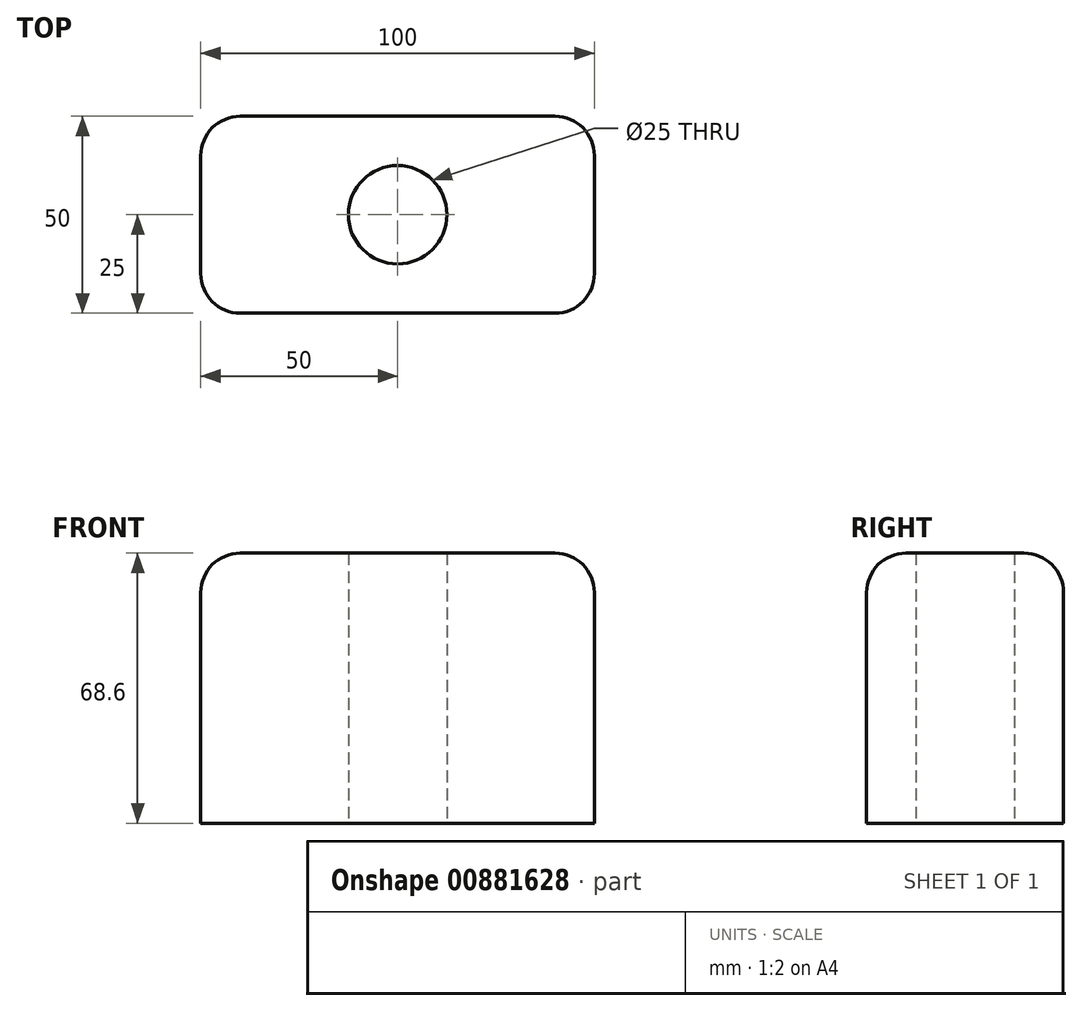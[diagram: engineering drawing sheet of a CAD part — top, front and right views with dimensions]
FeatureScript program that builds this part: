
annotation { "Feature Type Name" : "Feature", "Feature Type Description" : "" }
export const myFeature = defineFeature(function(context is Context, id is Id, definition is map)
    precondition{}
    {
        {
            var Q0;
            Q0=qCreatedBy(makeId("Top.planeOp"),FACE);
            var sketch = newSketch(context, id + "F0", { "sketchPlane" : qUnion([Q0])});
            skLineSegment(sketch, "E0.bottom", {"start": v(-50, 25) * mm, "end": v(50, 25) * mm});
            skLineSegment(sketch, "E0.top", {"start": v(-50, -25) * mm, "end": v(50, -25) * mm});
            skLineSegment(sketch, "E0.left", {"start": v(-50, 25) * mm, "end": v(-50, -25) * mm});
            skLineSegment(sketch, "E0.right", {"start": v(50, 25) * mm, "end": v(50, -25) * mm});
            skPoint(sketch, "E1", {"position": v(-50, 0) * mm});
            skPoint(sketch, "E2", {"position": v(0, 25) * mm});
            skCircle(sketch, "E3", {"center": v(0, 0) * mm, "radius": 12.5 * mm});
            skSolve(sketch);
        }
        {
            var Q0;
            Q0=makeQuery(id+"F0.imprint","IMPRINT",FACE,{"disambiguationData":[TD([[makeQuery(id+"F0.imprint","IMPRINT",EDGE,{"derivedFrom":sQuery(id+"F0.wireOp",EDGE,"E0.bottom")}),-1.0]])]});
            extrude(context, id + "F1", {"entities" : qUnion([Q0]), "depth" : 68.6 * mm, "offsetDistance" : 25 * mm});
        }
        {
            var Q0;
            Q0=makeQuery(id+"F1.opExtrude","CAP_EDGE",EDGE,{"disambiguationData":[OSD([sQuery(id+"F0.wireOp",EDGE,"E0.right")])],"isStart":false});
            var Q1;
            Q1=makeQuery(id+"F1.opExtrude","CAP_EDGE",EDGE,{"disambiguationData":[OSD([sQuery(id+"F0.wireOp",EDGE,"E0.top")])],"isStart":false});
            var Q2;
            Q2=makeQuery(id+"F1.opExtrude","CAP_EDGE",EDGE,{"disambiguationData":[OSD([sQuery(id+"F0.wireOp",EDGE,"E0.left")])],"isStart":false});
            var Q3;
            Q3=makeQuery(id+"F1.opExtrude","CAP_EDGE",EDGE,{"disambiguationData":[OSD([sQuery(id+"F0.wireOp",EDGE,"E0.bottom")])],"isStart":false});
            var Q4;
            Q4=makeQuery(id+"F1.opExtrude","SWEPT_EDGE",EDGE,{"disambiguationData":[OSD([sQuery(id+"F0.wireOp",EDGE,"E0.bottom"),sQuery(id+"F0.wireOp",EDGE,"E0.right")])]});
            var Q5;
            Q5=makeQuery(id+"F1.opExtrude","SWEPT_EDGE",EDGE,{"disambiguationData":[OSD([sQuery(id+"F0.wireOp",EDGE,"E0.top"),sQuery(id+"F0.wireOp",EDGE,"E0.right")])]});
            var Q6;
            Q6=makeQuery(id+"F1.opExtrude","SWEPT_EDGE",EDGE,{"disambiguationData":[OSD([sQuery(id+"F0.wireOp",EDGE,"E0.top"),sQuery(id+"F0.wireOp",EDGE,"E0.left")])]});
            var Q7;
            Q7=makeQuery(id+"F1.opExtrude","SWEPT_EDGE",EDGE,{"disambiguationData":[OSD([sQuery(id+"F0.wireOp",EDGE,"E0.bottom"),sQuery(id+"F0.wireOp",EDGE,"E0.left")])]});
            fillet(context, id + "F2", {"entities" : qUnion([Q0, Q1, Q2, Q3, Q4, Q5, Q6, Q7]), "radius" : 10 * mm, "tangentPropagation" : true, "allowEdgeOverflow" : false});
        }
    });
